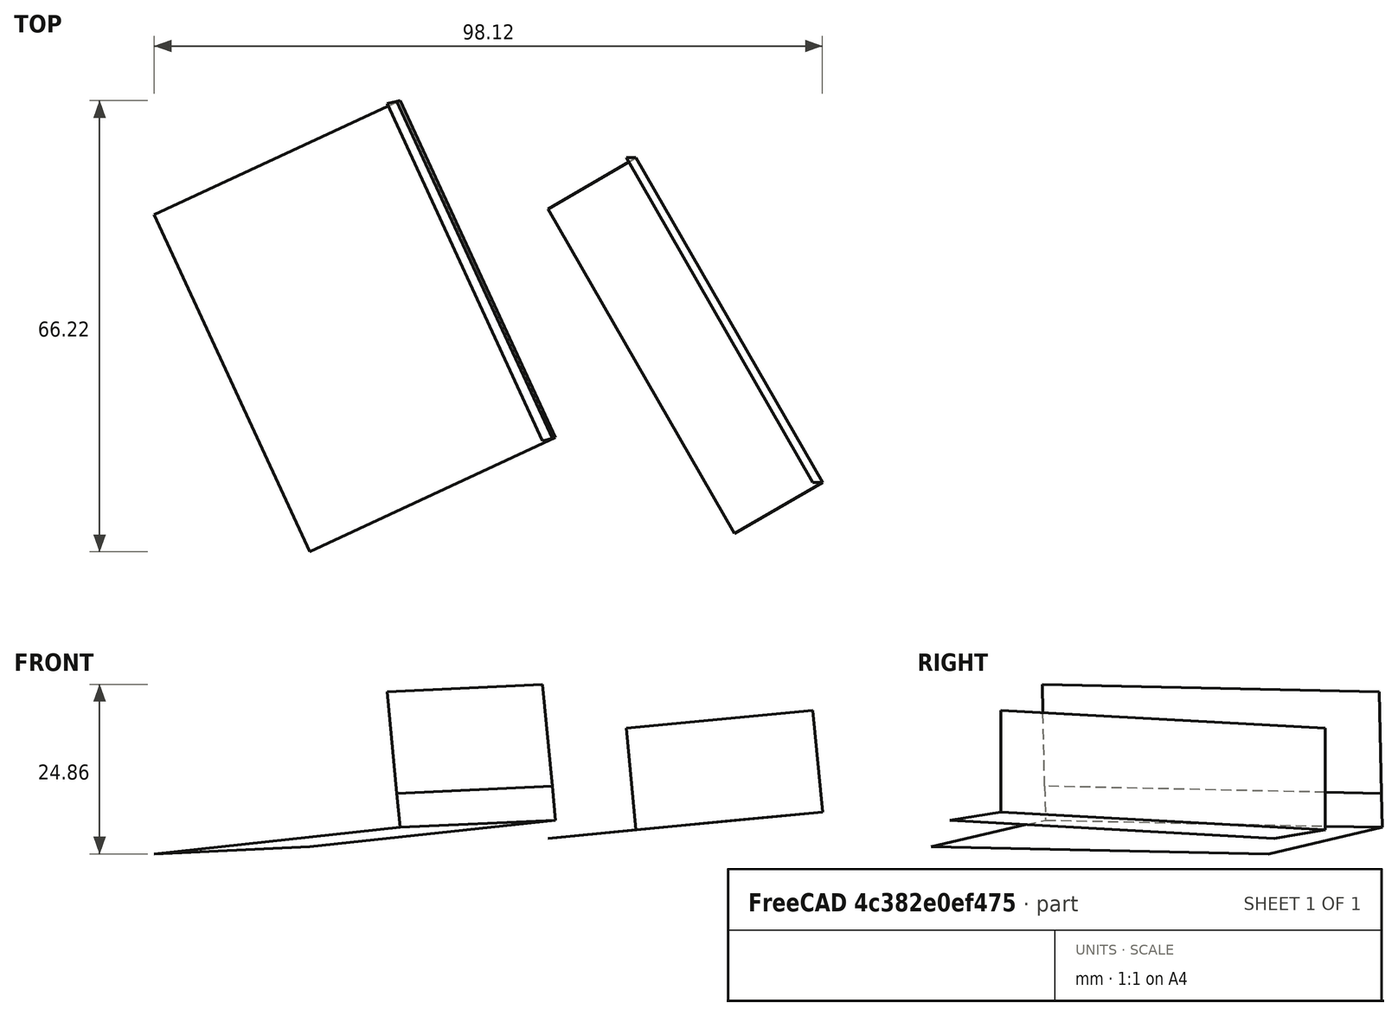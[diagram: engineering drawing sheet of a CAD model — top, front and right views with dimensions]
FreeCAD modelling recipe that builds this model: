
FCSTD DOCUMENT  (FreeCAD 0.19R24366 (Git))
Label: sailface_assembly_v2
License: All rights reserved
LicenseURL: http://en.wikipedia.org/wiki/All_rights_reserved
objects: Part::FeaturePython×7, App::Link×3, App::FeaturePython×2
note: 6 computed .brp shape members not serialized (recipe doc carries the construction recipe); baked Part::Feature solids carry a one-line shape summary decoded from their .brp
EXTERNAL_REF file=sailface_vertical_assembly_v1.FCStd obj=Part
EXTERNAL_REF file=sailface_steerage_assembly_v1.FCStd obj=Assembly
EXTERNAL_REF file=sailface_prop_motor_assembly.FCStd obj=Assembly001

FEATURE [App::FeaturePython] Constraints  # WARN: FeaturePython — macro-defined, semantics opaque (R4)
  _Version = 1
FEATURE [App::Link] Link  label="VerticalConnector"
  LinkPlacement = pos=(140.887,65.6727,-152.464) rot=(0.047485,-0.082247,-0.99548;1.05113rad)
  LinkedObject = -> <external sailface_vertical_assembly_v1.FCStd>#Part
  Placement = pos=(140.887,65.6727,-152.464) rot=(0.047485,-0.082247,-0.99548;1.05113rad)
FEATURE [App::Link] Link001  label="SteerageAssembly"
  LinkPlacement = pos=(0,0,0) rot=(0.707107,0,0.707107;0.633399rad)
  LinkedObject = -> <external sailface_steerage_assembly_v1.FCStd>#Assembly
  Placement = pos=(0,0,0) rot=(0.707107,0,0.707107;0.633399rad)
FEATURE [App::Link] Link002  label="PropMotorAssembly"
  LinkPlacement = pos=(0,0,0) rot=(0,1,0;1.309rad)
  LinkedObject = -> <external sailface_prop_motor_assembly.FCStd>#Assembly001
  Placement = pos=(0,0,0) rot=(0,1,0;1.309rad)
FEATURE [Part::FeaturePython] Parts  # WARN: FeaturePython — macro-defined, semantics opaque (R4)
  Group = -> [Link,Link001,Link002]
  GroupMode = 0
FEATURE [Part::FeaturePython] Assembly  label="InternalAssembly"  # WARN: FeaturePython — macro-defined, semantics opaque (R4)
  AutoRelax = true
  BuildShape = 0
  Freeze = false
  Group = -> [Constraints,Elements,Parts]
  Verbose = false
  _SolverType = 1
  _Version = 1
FEATURE [App::FeaturePython] Elements  # WARN: FeaturePython — macro-defined, semantics opaque (R4)
  Group = -> [_Element,_Element001,_Element002,_Element003,_Element004]
FEATURE [Part::FeaturePython] _Element  # link proxy (typed FeaturePython)
  Detach = false
  LinkTransform = true
  LinkedObject = -> Link [Body.Pad001.Face11]
  _Parent = -> Elements
FEATURE [Part::FeaturePython] _Element001  # link proxy (typed FeaturePython)
  Detach = false
  LinkTransform = true
  LinkedObject = -> Link001 [1.$Element.]
  _Parent = -> Elements
FEATURE [Part::FeaturePython] _Element002  # link proxy (typed FeaturePython)
  Detach = false
  LinkTransform = true
  LinkedObject = -> Link001 [1.$Element001.]
  _Parent = -> Elements
FEATURE [Part::FeaturePython] _Element003  # link proxy (typed FeaturePython)
  Detach = false
  LinkTransform = true
  LinkedObject = -> Link [Body.Pad001.Face7]
  _Parent = -> Elements
FEATURE [Part::FeaturePython] _Element004  # link proxy (typed FeaturePython)
  Detach = false
  LinkTransform = true
  LinkedObject = -> Link001 [1.$Element002.]
  _Parent = -> Elements

RESOLVED EXTERNAL PARTS (link-assembly join: the EXTERNAL_REF files above that resolve inside this repo's crawl, each included once):
---- part sailface_prop_motor_assembly.FCStd = doc fcstd_c044ced34071 ----
FCSTD DOCUMENT  (FreeCAD 0.19R24366 (Git))
Label: sailface_prop_motor_assembly
License: All rights reserved
LicenseURL: http://en.wikipedia.org/wiki/All_rights_reserved
objects: App::FeaturePython×23, Part::FeaturePython×17, App::Link×4
note: 16 computed .brp shape members not serialized (recipe doc carries the construction recipe); baked Part::Feature solids carry a one-line shape summary decoded from their .brp
EXTERNAL_REF file=Prop_uxcell_prop_shaft.FCStd obj=Part
EXTERNAL_REF file=Prop_uxcell_prop_shaft.FCStd obj=Part001
EXTERNAL_REF file=Prop_uxcell_prop_shaft.FCStd obj=Part002
EXTERNAL_REF file=MotorAndHolder_v1.FCStd obj=Part

FEATURE [App::Link] Link004  label="PropShaftSleeve"
  LinkPlacement = pos=(-1.04194e-10,303.325,152.862) rot=(0.782097,-0.530606,0.326776;2.24386rad)
  LinkedObject = -> <external Prop_uxcell_prop_shaft.FCStd>#Part
  Placement = pos=(-1.04194e-10,303.325,152.862) rot=(0.782097,-0.530606,0.326776;2.24386rad)
FEATURE [App::Link] Link005  label="PropAndShaft"
  LinkPlacement = pos=(1.45925,156.515,79.2819) rot=(0.211549,0.512519,0.832209;3.80335rad)
  LinkedObject = -> <external Prop_uxcell_prop_shaft.FCStd>#Part001
  Placement = pos=(1.45925,156.515,79.2819) rot=(0.211549,0.512519,0.832209;3.80335rad)
FEATURE [App::Link] Link015  label="ShaftConnectorTemp"
  LinkPlacement = pos=(1.74213e-10,0,0) rot=(-0.752268,-0.345496,-0.561003;1.37203rad)
  LinkedObject = -> <external Prop_uxcell_prop_shaft.FCStd>#Part002
  Placement = pos=(1.74213e-10,0,0) rot=(-0.752268,-0.345496,-0.561003;1.37203rad)
FEATURE [App::Link] Link014  label="MotorPart"
  LinkPlacement = pos=(9.7944e-11,0,0) rot=(-0.332635,0.494526,0.802993;2.15114rad)
  LinkedObject = -> <external MotorAndHolder_v1.FCStd>#Part
  Placement = pos=(9.7944e-11,0,0) rot=(-0.332635,0.494526,0.802993;2.15114rad)
FEATURE [Part::FeaturePython] Workplane  # WARN: FeaturePython — macro-defined, semantics opaque (R4)
  Fixed = true
  Length = 60.4603
  Placement = pos=(0,0,0) rot=(1,0,0;2.0376rad)
  Width = 60.4603
FEATURE [Part::FeaturePython] Parts001  # WARN: FeaturePython — macro-defined, semantics opaque (R4)
  Group = -> [Link014,Link015,Link005,Link004,Workplane]
  GroupMode = 0
FEATURE [Part::FeaturePython] _Element043  # link proxy (typed FeaturePython)
  Detach = false
  LinkTransform = true
  LinkedObject = -> Link004 [Extrude.Face2]
  _Parent = -> Elements001
FEATURE [App::FeaturePython] ElementLink018  label="_Element043"  # link proxy (typed FeaturePython)
  LinkTransform = true
  LinkedObject = -> _Element043
  _Parent = -> Constraint008
FEATURE [Part::FeaturePython] _Element044  # link proxy (typed FeaturePython)
  Detach = false
  LinkTransform = true
  LinkedObject = -> Link005 [Extrude002.Face1]
  _Parent = -> Elements001
FEATURE [App::FeaturePython] ElementLink019  label="_Element044"  # link proxy (typed FeaturePython)
  LinkTransform = true
  LinkedObject = -> _Element044
  _Parent = -> Constraint008
FEATURE [App::FeaturePython] Constraint008  label="AxialAlignment002"  # WARN: FeaturePython — macro-defined, semantics opaque (R4)
  Angle = 0
  AnglePitch = 0
  AngleRoll = 0
  Disabled = false
  Group = -> [ElementLink018,ElementLink019]
  LockAngle = false
  Multiply = false
  _ConstraintType = 36
  _Parent = -> Constraints001
FEATURE [App::FeaturePython] ElementLink020  label="_Element044"  # link proxy (typed FeaturePython)
  LinkTransform = true
  LinkedObject = -> _Element044
  _Parent = -> Constraint009
FEATURE [App::FeaturePython] ElementLink021  label="_Element043"  # link proxy (typed FeaturePython)
  LinkTransform = true
  LinkedObject = -> _Element043
  _Parent = -> Constraint009
FEATURE [App::FeaturePython] Constraint009  label="AxialAlignment"  # WARN: FeaturePython — macro-defined, semantics opaque (R4)
  Angle = 0
  AnglePitch = 0
  AngleRoll = 0
  Disabled = false
  Group = -> [ElementLink020,ElementLink021]
  LockAngle = false
  Multiply = false
  _ConstraintType = 36
  _Parent = -> Constraints001
FEATURE [Part::FeaturePython] _Element046  # link proxy (typed FeaturePython)
  Detach = false
  LinkTransform = true
  LinkedObject = -> Link005 [Extrude002.Face3]
  _Parent = -> Elements001
FEATURE [Part::FeaturePython] _Element045  # link proxy (typed FeaturePython)
  Detach = false
  LinkTransform = true
  LinkedObject = -> Link015 [Body.Pocket001.Face7]
  _Parent = -> Elements001
FEATURE [Part::FeaturePython] _Element047  # link proxy (typed FeaturePython)
  Detach = false
  LinkTransform = true
  LinkedObject = -> Link014 [Body.Pocket.Face11]
  _Parent = -> Elements001
FEATURE [Part::FeaturePython] _Element048  # link proxy (typed FeaturePython)
  Detach = false
  LinkTransform = true
  LinkedObject = -> Link015 [Body.Pocket001.Face6]
  _Parent = -> Elements001
FEATURE [App::FeaturePython] Constraints001  # WARN: FeaturePython — macro-defined, semantics opaque (R4)
  Group = -> [Constraint008,Constraint009,Constraint,Constraint010,Constraint011,Constraint012,Constraint013]
  _Version = 1
FEATURE [App::FeaturePython] Elements001  # WARN: FeaturePython — macro-defined, semantics opaque (R4)
  Group = -> [_Element043,_Element044,_Element045,_Element046,_Element047,_Element048,Element,Element001,Element002,Element003,Element004,_Element,_Element049,_Element050]
FEATURE [Part::FeaturePython] Assembly001  label="PropMotorAssembly"  # WARN: FeaturePython — macro-defined, semantics opaque (R4)
  AutoRelax = true
  BuildShape = 0
  Freeze = false
  Group = -> [Constraints001,Parts001,Elements001]
  Verbose = false
  _SolverType = 1
  _Version = 1
FEATURE [Part::FeaturePython] Element  # link proxy (typed FeaturePython)
  Detach = false
  LinkTransform = true
  LinkedObject = -> Link014 [Body.Pocket.Face5]
  _Parent = -> Elements001
FEATURE [Part::FeaturePython] Element001  # link proxy (typed FeaturePython)
  Detach = false
  LinkTransform = true
  LinkedObject = -> Link014 [Body.Pocket.Face3]
  _Parent = -> Elements001
FEATURE [Part::FeaturePython] Element002  # link proxy (typed FeaturePython)
  Detach = false
  LinkTransform = true
  LinkedObject = -> Link014 [Body.Pocket.Face10]
  _Parent = -> Elements001
FEATURE [Part::FeaturePython] Element003  # link proxy (typed FeaturePython)
  Detach = false
  LinkTransform = true
  LinkedObject = -> Link014 [Body.Pocket.Face6]
  _Parent = -> Elements001
FEATURE [Part::FeaturePython] Element004  # link proxy (typed FeaturePython)
  Detach = false
  LinkTransform = true
  LinkedObject = -> Link014 [Body.Pocket.Face4]
  _Parent = -> Elements001
FEATURE [App::FeaturePython] Constraint  label="AxialAlignment003"  # WARN: FeaturePython — macro-defined, semantics opaque (R4)
  Angle = 0
  AnglePitch = 0
  AngleRoll = 0
  Disabled = false
  Group = -> [ElementLink,ElementLink022]
  LockAngle = false
  Multiply = false
  _ConstraintType = 36
  _Parent = -> Constraints001
FEATURE [App::FeaturePython] ElementLink  label="_Element"  # link proxy (typed FeaturePython)
  LinkTransform = true
  LinkedObject = -> _Element
  _Parent = -> Constraint
FEATURE [Part::FeaturePython] _Element  # link proxy (typed FeaturePython)
  Detach = false
  LinkTransform = true
  LinkedObject = -> Link015 [Body.Pocket001.Face4]
  _Parent = -> Elements001
FEATURE [App::FeaturePython] ElementLink022  label="Element002"  # link proxy (typed FeaturePython)
  LinkTransform = true
  LinkedObject = -> Element002
  _Parent = -> Constraint
FEATURE [App::FeaturePython] Constraint010  label="AxialAlignment004"  # WARN: FeaturePython — macro-defined, semantics opaque (R4)
  Angle = 0
  AnglePitch = 0
  AngleRoll = 0
  Disabled = false
  Group = -> [ElementLink023,ElementLink024]
  LockAngle = false
  Multiply = false
  _ConstraintType = 36
  _Parent = -> Constraints001
FEATURE [App::FeaturePython] ElementLink023  label="_Element044"  # link proxy (typed FeaturePython)
  LinkTransform = true
  LinkedObject = -> _Element044
  _Parent = -> Constraint010
FEATURE [App::FeaturePython] ElementLink024  label="_Element"  # link proxy (typed FeaturePython)
  LinkTransform = true
  LinkedObject = -> _Element
  _Parent = -> Constraint010
FEATURE [App::FeaturePython] Constraint011  label="AxialAlignment005"  # WARN: FeaturePython — macro-defined, semantics opaque (R4)
  Angle = 0
  AnglePitch = 0
  AngleRoll = 0
  Disabled = false
  Group = -> [ElementLink025,ElementLink026]
  LockAngle = false
  Multiply = false
  _ConstraintType = 36
  _Parent = -> Constraints001
FEATURE [App::FeaturePython] ElementLink025  label="_Element049"  # link proxy (typed FeaturePython)
  LinkTransform = true
  LinkedObject = -> _Element049
  _Parent = -> Constraint011
FEATURE [Part::FeaturePython] _Element049  # link proxy (typed FeaturePython)
  Detach = false
  LinkTransform = true
  LinkedObject = -> Workplane [Face1]
  _Parent = -> Elements001
FEATURE [App::FeaturePython] ElementLink026  label="_Element050"  # link proxy (typed FeaturePython)
  LinkTransform = true
  LinkedObject = -> _Element050
  _Parent = -> Constraint011
FEATURE [Part::FeaturePython] _Element050  # link proxy (typed FeaturePython)
  Detach = false
  LinkTransform = true
  LinkedObject = -> Link014 [Body.Pocket.Face2]
  _Parent = -> Elements001
FEATURE [App::FeaturePython] Constraint012  label="PlaneCoincident"  # WARN: FeaturePython — macro-defined, semantics opaque (R4)
  Angle = 0
  AnglePitch = 0
  AngleRoll = 0
  Cascade = false
  Disabled = false
  Group = -> [ElementLink027,ElementLink028]
  LockAngle = false
  Multiply = false
  OffsetX = 0
  OffsetY = 0
  _ConstraintType = 35
  _Parent = -> Constraints001
FEATURE [App::FeaturePython] ElementLink027  label="_Element047"  # link proxy (typed FeaturePython)
  LinkTransform = true
  LinkedObject = -> _Element047
  _Parent = -> Constraint012
FEATURE [App::FeaturePython] ElementLink028  label="_Element045"  # link proxy (typed FeaturePython)
  LinkTransform = true
  LinkedObject = -> _Element045
  _Parent = -> Constraint012
FEATURE [App::FeaturePython] Constraint013  label="PlaneCoincident001"  # WARN: FeaturePython — macro-defined, semantics opaque (R4)
  Angle = 0
  AnglePitch = 0
  AngleRoll = 0
  Cascade = false
  Disabled = true
  Group = -> [ElementLink029,ElementLink030]
  LockAngle = false
  Multiply = false
  OffsetX = 0
  OffsetY = 0
  _ConstraintType = 35
  _Parent = -> Constraints001
FEATURE [App::FeaturePython] ElementLink029  label="_Element046"  # link proxy (typed FeaturePython)
  LinkTransform = true
  LinkedObject = -> _Element046
  _Parent = -> Constraint013
FEATURE [App::FeaturePython] ElementLink030  label="_Element045"  # link proxy (typed FeaturePython)
  LinkTransform = true
  LinkedObject = -> _Element045
  _Parent = -> Constraint013
---- part sailface_steerage_assembly_v1.FCStd = doc fcstd_398bf6237f52 ----
FCSTD DOCUMENT  (FreeCAD 0.19R24366 (Git))
Label: sailface_steerage_assembly_v1
License: All rights reserved
LicenseURL: http://en.wikipedia.org/wiki/All_rights_reserved
objects: App::FeaturePython×20, Part::FeaturePython×17, App::Link×5
note: 16 computed .brp shape members not serialized (recipe doc carries the construction recipe); baked Part::Feature solids carry a one-line shape summary decoded from their .brp
EXTERNAL_REF file=rudder_coarse_1.FCStd obj=Part
EXTERNAL_REF file=ServoSunFinderSF3218MG.FCStd obj=Part002
EXTERNAL_REF file=ServoSunFinderSF3218MG.FCStd obj=Part
EXTERNAL_REF file=ServoSunFinderSF3218MG.FCStd obj=Part001
EXTERNAL_REF file=ServoSunFinderSF3218MG.FCStd obj=Part003

FEATURE [App::Link] Link002  label="PartRudderWithPost"
  LinkPlacement = pos=(-77.119,-40.9847,81.721) rot=(0.845448,-0.472566,-0.248797;1.29098rad)
  LinkedObject = -> <external rudder_coarse_1.FCStd>#Part
  Placement = pos=(-77.119,-40.9847,81.721) rot=(0.845448,-0.472566,-0.248797;1.29098rad)
FEATURE [App::Link] Link003  label="ServoHorn001"
  LinkPlacement = pos=(79.208,1.37065,-28.7732) rot=(-0.078576,0.224256,0.971357;2.48549rad)
  LinkedObject = -> <external ServoSunFinderSF3218MG.FCStd>#Part002
  Placement = pos=(79.208,1.37065,-28.7732) rot=(-0.078576,0.224256,0.971357;2.48549rad)
FEATURE [App::Link] Link004  label="Servo_SF3218MG001"
  LinkPlacement = pos=(0,0,0) rot=(-1,0,0;0.453786rad)
  LinkedObject = -> <external ServoSunFinderSF3218MG.FCStd>#Part
  Placement = pos=(0,0,0) rot=(-1,0,0;0.453786rad)
FEATURE [App::Link] Link005  label="ServoHolderPart"
  LinkPlacement = pos=(0,0,0) rot=(1,0,0;0.456494rad)
  LinkedObject = -> <external ServoSunFinderSF3218MG.FCStd>#Part001
  Placement = pos=(0,0,0) rot=(1,0,0;0.456494rad)
FEATURE [App::Link] Link006  label="PostHoleJacket"
  LinkPlacement = pos=(-54.4606,-25.4419,-34.4738) rot=(-0.993805,-0.11009,0.015223;0.456404rad)
  LinkedObject = -> <external ServoSunFinderSF3218MG.FCStd>#Part003
  Placement = pos=(-54.4606,-25.4419,-34.4738) rot=(-0.993805,-0.11009,0.015223;0.456404rad)
FEATURE [Part::FeaturePython] Parts  # WARN: FeaturePython — macro-defined, semantics opaque (R4)
  Group = -> [Link002,Link003,Link004,Link005,Link006]
  GroupMode = 0
FEATURE [Part::FeaturePython] Assembly  label="SteerageAssembly"  # WARN: FeaturePython — macro-defined, semantics opaque (R4)
  AutoRelax = true
  BuildShape = 0
  Freeze = false
  Group = -> [Constraints,Elements,Parts,Relations]
  Verbose = false
  _SolverType = 1
  _Version = 1
FEATURE [App::FeaturePython] Constraints  # WARN: FeaturePython — macro-defined, semantics opaque (R4)
  Group = -> [Constraint001,Constraint002,Constraint,Constraint004]
  _Version = 1
FEATURE [App::FeaturePython] Elements  # WARN: FeaturePython — macro-defined, semantics opaque (R4)
  Group = -> [_Element,_Element002,_Element003,_Element004,_Element005,_Element008,_Element022,_Element024,Element,Element001,Element002,_Element025,_Element026,_Element027,_Element028]
FEATURE [Part::FeaturePython] _Element  # link proxy (typed FeaturePython)
  Detach = false
  LinkTransform = true
  LinkedObject = -> Link002 [Extrude001.Face1]
  _Parent = -> Elements
FEATURE [Part::FeaturePython] _Element002  # link proxy (typed FeaturePython)
  Detach = false
  LinkTransform = true
  LinkedObject = -> Link004 [Solid.Face66]
  _Parent = -> Elements
FEATURE [Part::FeaturePython] _Element003  # link proxy (typed FeaturePython)
  Detach = false
  LinkTransform = true
  LinkedObject = -> Link003 [Solid001.Face34]
  _Parent = -> Elements
FEATURE [App::FeaturePython] Constraint001  label="PlaneCoincident"  # WARN: FeaturePython — macro-defined, semantics opaque (R4)
  Angle = 0
  AnglePitch = 0
  AngleRoll = 0
  Cascade = false
  Disabled = true
  Group = -> [ElementLink002,ElementLink003]
  LockAngle = false
  Multiply = false
  OffsetX = 0
  OffsetY = 0
  _ConstraintType = 35
  _Parent = -> Constraints
FEATURE [App::FeaturePython] ElementLink002  label="_Element002"  # link proxy (typed FeaturePython)
  LinkTransform = true
  LinkedObject = -> _Element002
  _Parent = -> Constraint001
FEATURE [App::FeaturePython] ElementLink003  label="_Element003"  # link proxy (typed FeaturePython)
  LinkTransform = true
  LinkedObject = -> _Element003
  _Parent = -> Constraint001
FEATURE [App::FeaturePython] Constraint002  label="AxialAlignment001"  # WARN: FeaturePython — macro-defined, semantics opaque (R4)
  Angle = 0
  AnglePitch = 0
  AngleRoll = 0
  Disabled = true
  Group = -> [ElementLink004,ElementLink005]
  LockAngle = false
  Multiply = false
  _ConstraintType = 36
  _Parent = -> Constraints
FEATURE [App::FeaturePython] ElementLink004  label="_Element004"  # link proxy (typed FeaturePython)
  LinkTransform = true
  LinkedObject = -> _Element004
  _Parent = -> Constraint002
FEATURE [Part::FeaturePython] _Element004  # link proxy (typed FeaturePython)
  Detach = false
  LinkTransform = true
  LinkedObject = -> Link006 [Body002.Pocket003.Face4]
  _Parent = -> Elements
FEATURE [App::FeaturePython] ElementLink005  label="_Element"  # link proxy (typed FeaturePython)
  LinkTransform = true
  LinkedObject = -> _Element
  _Parent = -> Constraint002
FEATURE [Part::FeaturePython] _Element005  # link proxy (typed FeaturePython)
  Detach = false
  LinkTransform = true
  LinkedObject = -> Link004 [Solid.Face27]
  _Parent = -> Elements
FEATURE [Part::FeaturePython] _Element008  # link proxy (typed FeaturePython)
  Detach = false
  LinkTransform = true
  LinkedObject = -> Link004 [Solid.Face33]
  _Parent = -> Elements
FEATURE [Part::FeaturePython] _Element022  # link proxy (typed FeaturePython)
  Detach = false
  LinkTransform = true
  LinkedObject = -> Link006 [Body002.Pocket003.Face1]
  _Parent = -> Elements
FEATURE [Part::FeaturePython] _Element024  label="YZ_Plane@PartRudderWithPost"  # link proxy (typed FeaturePython)
  Detach = false
  LinkTransform = true
  LinkedObject = -> Link002 [Origin.YZ_Plane.]
  _Parent = -> Elements
FEATURE [Part::FeaturePython] Element  # link proxy (typed FeaturePython)
  Detach = false
  LinkTransform = true
  LinkedObject = -> Link005 [Body001.Pad010.Face42]
  _Parent = -> Elements
FEATURE [Part::FeaturePython] Element001  # link proxy (typed FeaturePython)
  Detach = false
  LinkTransform = true
  LinkedObject = -> Link005 [Body001.Pad010.Face36]
  _Parent = -> Elements
FEATURE [Part::FeaturePython] Element002  # link proxy (typed FeaturePython)
  Detach = false
  LinkTransform = true
  LinkedObject = -> Link005 [Body001.Pad010.Face39]
  _Parent = -> Elements
FEATURE [App::FeaturePython] Constraint  label="AxialAlignment"  # WARN: FeaturePython — macro-defined, semantics opaque (R4)
  Angle = 0
  AnglePitch = 0
  AngleRoll = 0
  Disabled = true
  Group = -> [ElementLink,ElementLink006]
  LockAngle = false
  Multiply = false
  _ConstraintType = 36
  _Parent = -> Constraints
FEATURE [App::FeaturePython] ElementLink  label="_Element022"  # link proxy (typed FeaturePython)
  LinkTransform = true
  LinkedObject = -> _Element022
  _Parent = -> Constraint
FEATURE [App::FeaturePython] ElementLink006  label="_Element025"  # link proxy (typed FeaturePython)
  LinkTransform = true
  LinkedObject = -> _Element025
  _Parent = -> Constraint
FEATURE [Part::FeaturePython] _Element025  # link proxy (typed FeaturePython)
  Detach = false
  LinkTransform = true
  LinkedObject = -> Link005 [Body001.Pad010.Face6]
  _Parent = -> Elements
FEATURE [Part::FeaturePython] _Element026  # link proxy (typed FeaturePython)
  Detach = false
  LinkTransform = true
  LinkedObject = -> Link004 [Solid.Face107]
  _Parent = -> Elements
FEATURE [Part::FeaturePython] _Element027  # link proxy (typed FeaturePython)
  Detach = false
  LinkTransform = true
  LinkedObject = -> Link005 [Body001.Pad010.Face23]
  _Parent = -> Elements
FEATURE [App::FeaturePython] Constraint004  label="PlaneCoincident001"  # WARN: FeaturePython — macro-defined, semantics opaque (R4)
  Angle = 0
  AnglePitch = 0
  AngleRoll = 0
  Cascade = false
  Disabled = true
  Group = -> [ElementLink009,ElementLink010]
  LockAngle = false
  Multiply = false
  OffsetX = 0
  OffsetY = 0
  _ConstraintType = 35
  _Parent = -> Constraints
FEATURE [App::FeaturePython] ElementLink009  label="_Element028"  # link proxy (typed FeaturePython)
  LinkTransform = true
  LinkedObject = -> _Element028
  _Parent = -> Constraint004
FEATURE [Part::FeaturePython] _Element028  # link proxy (typed FeaturePython)
  Detach = false
  LinkTransform = true
  LinkedObject = -> Link005 [Body001.Pad010.Face21]
  _Parent = -> Elements
FEATURE [App::FeaturePython] ElementLink010  label="_Element008"  # link proxy (typed FeaturePython)
  LinkTransform = true
  LinkedObject = -> _Element008
  _Parent = -> Constraint004
FEATURE [App::FeaturePython] Relations  # WARN: FeaturePython — macro-defined, semantics opaque (R4)
  Constraints = -> Constraints
  Group = -> [Relation,Relation001,Relation002,Relation003,Relation004]
FEATURE [App::FeaturePython] Relation  label="PartRudderWithPost"  # WARN: FeaturePython — macro-defined, semantics opaque (R4)
  Count = 0
  Group = -> [Constraint002]
  Index = 0
  Part = -> Link002
FEATURE [App::FeaturePython] Relation001  label="ServoHorn001"  # WARN: FeaturePython — macro-defined, semantics opaque (R4)
  Count = 0
  Group = -> [Constraint001]
  Index = 0
  Part = -> Link003
FEATURE [App::FeaturePython] Relation002  label="Servo_SF3218MG001"  # WARN: FeaturePython — macro-defined, semantics opaque (R4)
  Count = 0
  Group = -> [Constraint001,Constraint004]
  Index = 0
  Part = -> Link004
FEATURE [App::FeaturePython] Relation003  label="ServoHolderPart"  # WARN: FeaturePython — macro-defined, semantics opaque (R4)
  Count = 0
  Group = -> [Constraint,Constraint004]
  Index = 0
  Part = -> Link005
FEATURE [App::FeaturePython] Relation004  label="PostHoleJacket"  # WARN: FeaturePython — macro-defined, semantics opaque (R4)
  Count = 0
  Group = -> [Constraint002,Constraint]
  Index = 0
  Part = -> Link006
